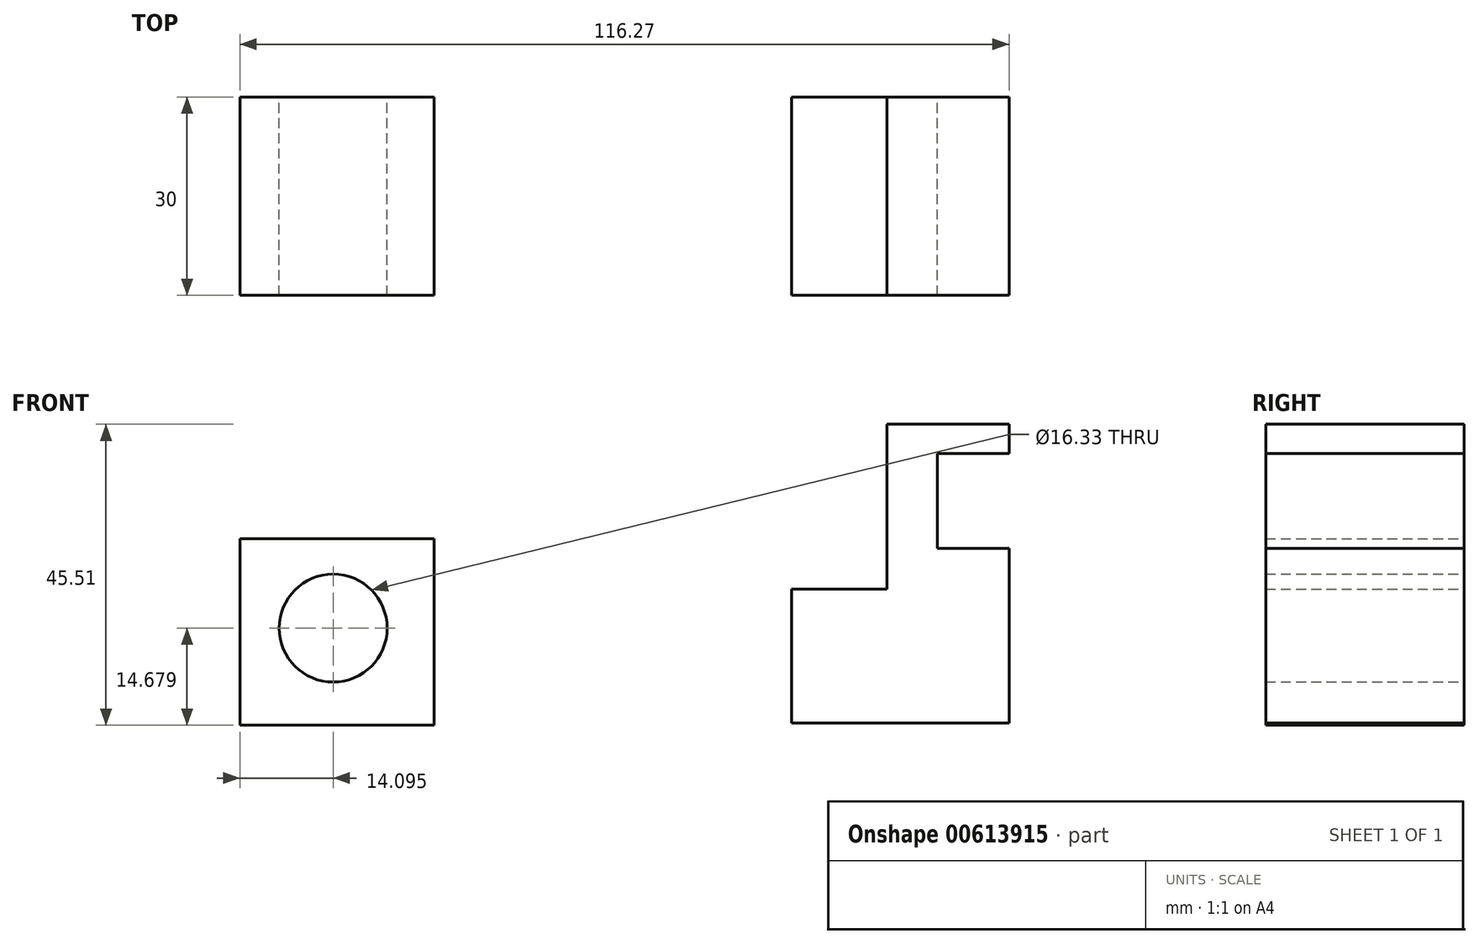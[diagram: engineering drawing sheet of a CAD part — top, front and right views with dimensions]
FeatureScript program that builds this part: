
annotation { "Feature Type Name" : "Feature", "Feature Type Description" : "" }
export const myFeature = defineFeature(function(context is Context, id is Id, definition is map)
    precondition{}
    {
        {
            var Q0;
            Q0=qCreatedBy(makeId("Front.planeOp"),FACE);
            var sketch = newSketch(context, id + "F0", { "sketchPlane" : qUnion([Q0])});
            skLineSegment(sketch, "E0.bottom", {"start": v(-57.1, 33.77) * mm, "end": v(-27.75, 33.77) * mm});
            skLineSegment(sketch, "E0.top", {"start": v(-57.1, 5.58) * mm, "end": v(-27.75, 5.58) * mm});
            skLineSegment(sketch, "E0.left", {"start": v(-57.1, 33.77) * mm, "end": v(-57.1, 5.58) * mm});
            skLineSegment(sketch, "E0.right", {"start": v(-27.75, 33.77) * mm, "end": v(-27.75, 5.58) * mm});
            skCircle(sketch, "E1", {"center": v(-43.01, 20.26) * mm, "radius": 8.16 * mm});
            skLineSegment(sketch, "E2.bottom", {"start": v(26.28, 26.13) * mm, "end": v(40.67, 26.13) * mm});
            skLineSegment(sketch, "E2.top", {"start": v(26.28, 5.87) * mm, "end": v(59.16, 5.87) * mm});
            skLineSegment(sketch, "E2.left", {"start": v(26.28, 26.13) * mm, "end": v(26.28, 5.87) * mm});
            skLineSegment(sketch, "E2.right", {"start": v(59.16, 26.13) * mm, "end": v(59.16, 5.87) * mm});
            skLineSegment(sketch, "E3.top", {"start": v(59.16, 32.3) * mm, "end": v(48.3, 32.3) * mm});
            skLineSegment(sketch, "E3.left", {"start": v(59.16, 26.13) * mm, "end": v(59.16, 32.3) * mm});
            skLineSegment(sketch, "E3.right", {"start": v(40.67, 26.13) * mm, "end": v(40.67, 32.3) * mm});
            skLineSegment(sketch, "E4.top", {"start": v(40.67, 51.09) * mm, "end": v(48.3, 51.09) * mm});
            skLineSegment(sketch, "E4.left", {"start": v(40.67, 32.3) * mm, "end": v(40.67, 51.09) * mm});
            skLineSegment(sketch, "E4.right", {"start": v(48.3, 32.3) * mm, "end": v(48.3, 46.68) * mm});
            skLineSegment(sketch, "E5.bottom", {"start": v(48.3, 51.09) * mm, "end": v(59.16, 51.09) * mm});
            skLineSegment(sketch, "E5.top", {"start": v(48.3, 46.68) * mm, "end": v(59.16, 46.68) * mm});
            skLineSegment(sketch, "E5.right", {"start": v(59.16, 51.09) * mm, "end": v(59.16, 46.68) * mm});
            skSolve(sketch);
        }
        {
            var Q0;
            Q0 = qSketchRegion(id + "F0", true);
            extrude(context, id + "F1", {"entities" : qUnion([Q0]), "depth" : 30 * mm, "offsetDistance" : 25.4 * mm});
        }
    });
